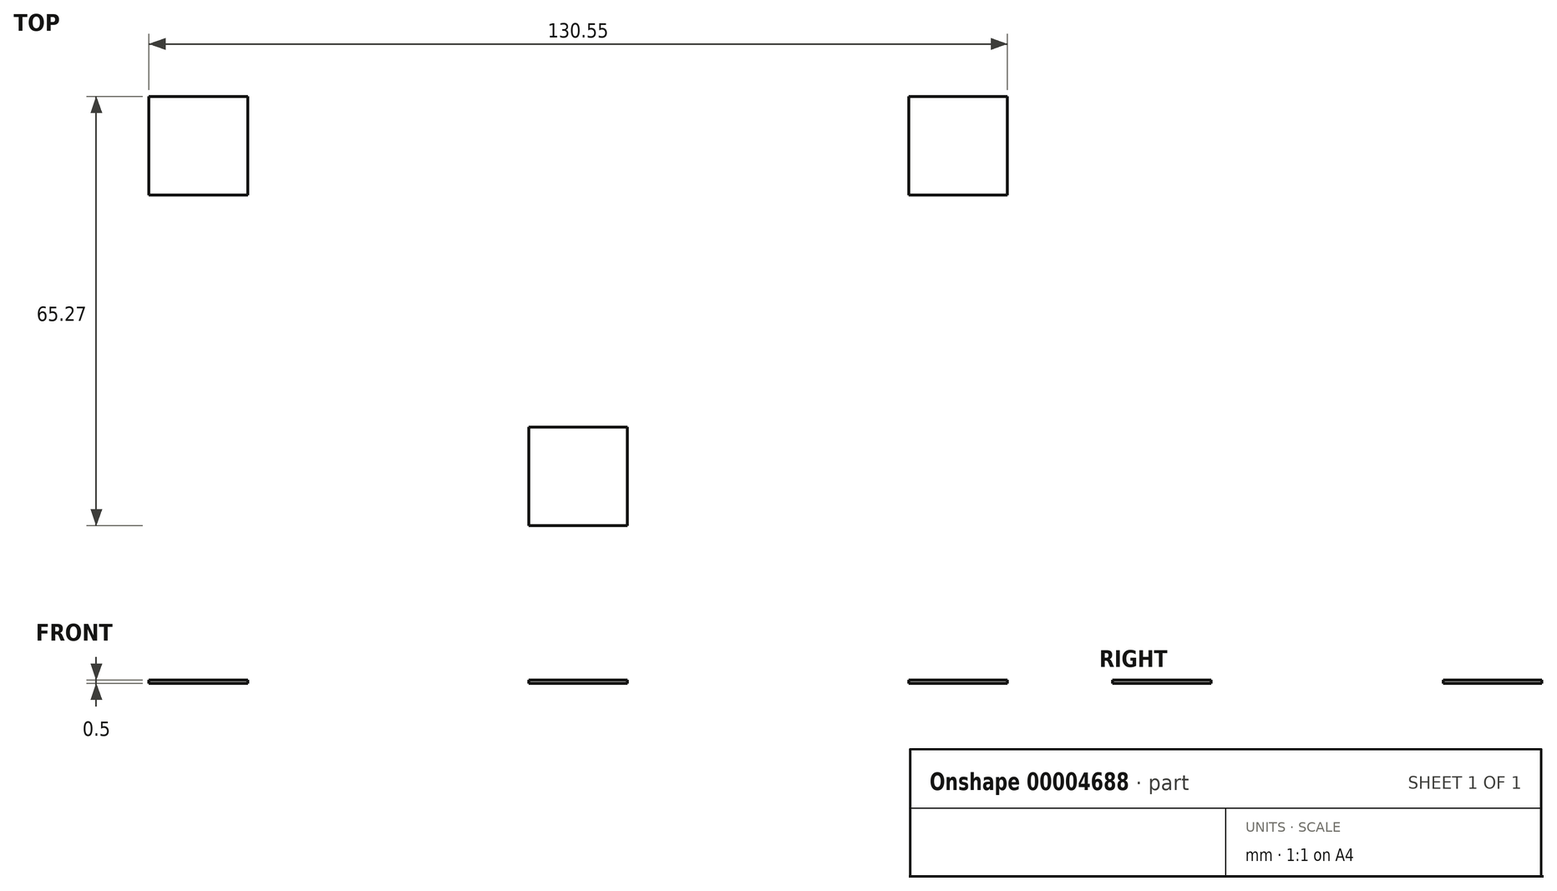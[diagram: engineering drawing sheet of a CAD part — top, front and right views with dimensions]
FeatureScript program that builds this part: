
annotation { "Feature Type Name" : "Feature", "Feature Type Description" : "" }
export const myFeature = defineFeature(function(context is Context, id is Id, definition is map)
    precondition{}
    {
        {
            var Q0;
            Q0=qCreatedBy(makeId("Top.planeOp"),FACE);
            var sketch = newSketch(context, id + "F0", { "sketchPlane" : qUnion([Q0])});
            skLineSegment(sketch, "E0.bottom", {"start": v(-53.29, 57.76) * mm, "end": v(-68.29, 57.76) * mm});
            skLineSegment(sketch, "E0.top", {"start": v(-53.29, 42.76) * mm, "end": v(-68.29, 42.76) * mm});
            skLineSegment(sketch, "E0.left", {"start": v(-53.29, 57.76) * mm, "end": v(-53.29, 42.76) * mm});
            skLineSegment(sketch, "E0.right", {"start": v(-68.29, 57.76) * mm, "end": v(-68.29, 42.76) * mm});
            skLineSegment(sketch, "E1.bottom", {"start": v(62.26, 57.76) * mm, "end": v(47.26, 57.76) * mm});
            skLineSegment(sketch, "E1.top", {"start": v(62.26, 42.76) * mm, "end": v(47.26, 42.76) * mm});
            skLineSegment(sketch, "E1.left", {"start": v(62.26, 57.76) * mm, "end": v(62.26, 42.76) * mm});
            skLineSegment(sketch, "E1.right", {"start": v(47.26, 57.76) * mm, "end": v(47.26, 42.76) * mm});
            skLineSegment(sketch, "E2.bottom", {"start": v(4.49, 7.49) * mm, "end": v(-10.51, 7.49) * mm});
            skLineSegment(sketch, "E2.top", {"start": v(4.49, -7.51) * mm, "end": v(-10.51, -7.51) * mm});
            skLineSegment(sketch, "E2.left", {"start": v(4.49, 7.49) * mm, "end": v(4.49, -7.51) * mm});
            skLineSegment(sketch, "E2.right", {"start": v(-10.51, 7.49) * mm, "end": v(-10.51, -7.51) * mm});
            skLineSegment(sketch, "E3", {"start": v(-53.29, 57.76) * mm, "end": v(-3.01, 57.76) * mm, "construction": true});
            skLineSegment(sketch, "E4", {"start": v(-3.01, 57.76) * mm, "end": v(47.26, 57.76) * mm, "construction": true});
            skLineSegment(sketch, "E5", {"start": v(-3.01, 57.76) * mm, "end": v(-3.01, 7.49) * mm, "construction": true});
            skSolve(sketch);
        }
        {
            var Q0;
            Q0 = qSketchRegion(id + "F0", true);
            extrude(context, id + "F1", {"entities" : qUnion([Q0]), "depth" : 0.5 * mm});
        }
    });
